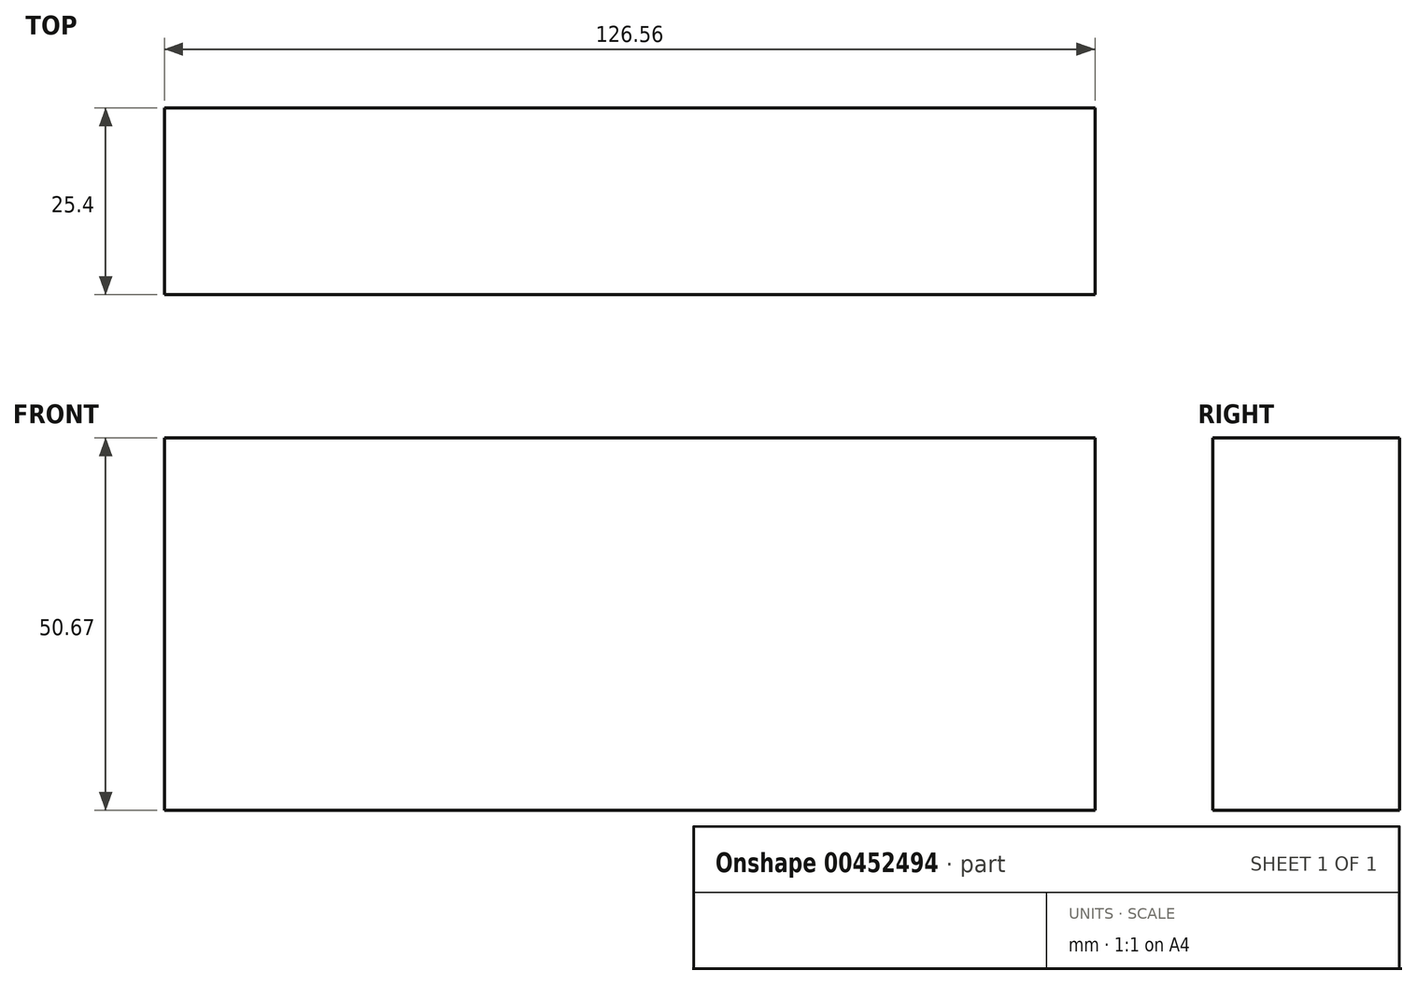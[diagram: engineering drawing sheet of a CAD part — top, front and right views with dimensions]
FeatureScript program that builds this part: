
annotation { "Feature Type Name" : "Feature", "Feature Type Description" : "" }
export const myFeature = defineFeature(function(context is Context, id is Id, definition is map)
    precondition{}
    {
        {
            var Q0;
            Q0=qCreatedBy(makeId("Front.planeOp"),FACE);
            var sketch = newSketch(context, id + "F0", { "sketchPlane" : qUnion([Q0])});
            skLineSegment(sketch, "E0.bottom", {"start": v(48.7, -50.67) * mm, "end": v(-77.86, -50.67) * mm});
            skLineSegment(sketch, "E0.top", {"start": v(48.7, 0) * mm, "end": v(-77.86, 0) * mm});
            skLineSegment(sketch, "E0.left", {"start": v(48.7, -50.67) * mm, "end": v(48.7, 0) * mm});
            skLineSegment(sketch, "E0.right", {"start": v(-77.86, -50.67) * mm, "end": v(-77.86, 0) * mm});
            skLineSegment(sketch, "E1.bottom", {"start": v(48.7, -50.67) * mm, "end": v(48.7, -50.67) * mm});
            skLineSegment(sketch, "E1.top", {"start": v(48.7, -50.67) * mm, "end": v(48.7, -50.67) * mm});
            skLineSegment(sketch, "E1.left", {"start": v(48.7, -50.67) * mm, "end": v(48.7, -50.67) * mm});
            skLineSegment(sketch, "E1.right", {"start": v(48.7, -50.67) * mm, "end": v(48.7, -50.67) * mm});
            skSolve(sketch);
        }
        {
            var Q0;
            Q0=makeQuery(id+"F0.imprint","IMPRINT",FACE,{"disambiguationData":[TD([[makeQuery(id+"F0.imprint","IMPRINT",EDGE,{"derivedFrom":sQuery(id+"F0.wireOp",EDGE,"E0.bottom")}),-1.0]])]});
            extrude(context, id + "F1", {"entities" : qUnion([Q0]), "depth" : 25.4 * mm});
        }
    });
